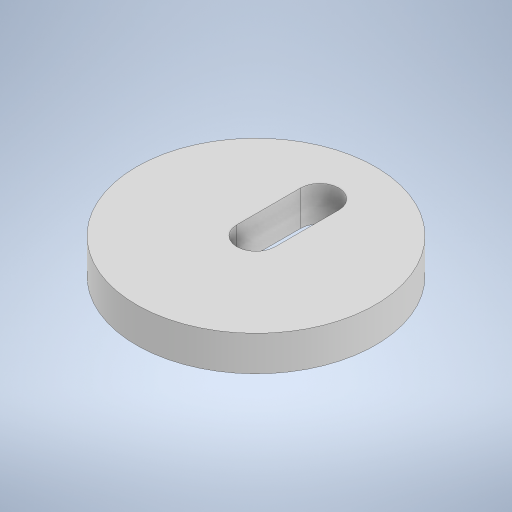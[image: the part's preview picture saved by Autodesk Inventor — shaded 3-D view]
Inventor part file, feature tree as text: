
AUTODESK INVENTOR PART (.ipt)
format: ipt  version: 2024.1 (Build 281209000, 209)  size: 302,080 bytes
history: native  units: mm
features: extrude x2, sketch x2, other x1
ambient origin geometry x8: Origin, YZ Plane, XZ Plane, XY Plane, X Axis, Y Axis, Z Axis, Center Point
bodies: Body1 (feature_tree)
feature tree (5):
  other  "ソリッド1"
  extrude  "押し出し1"  Depth=45.0mm
  extrude  "押し出し2"  Depth=51.0mm
  sketch  "スケッチ1"
  sketch  "スケッチ2"
